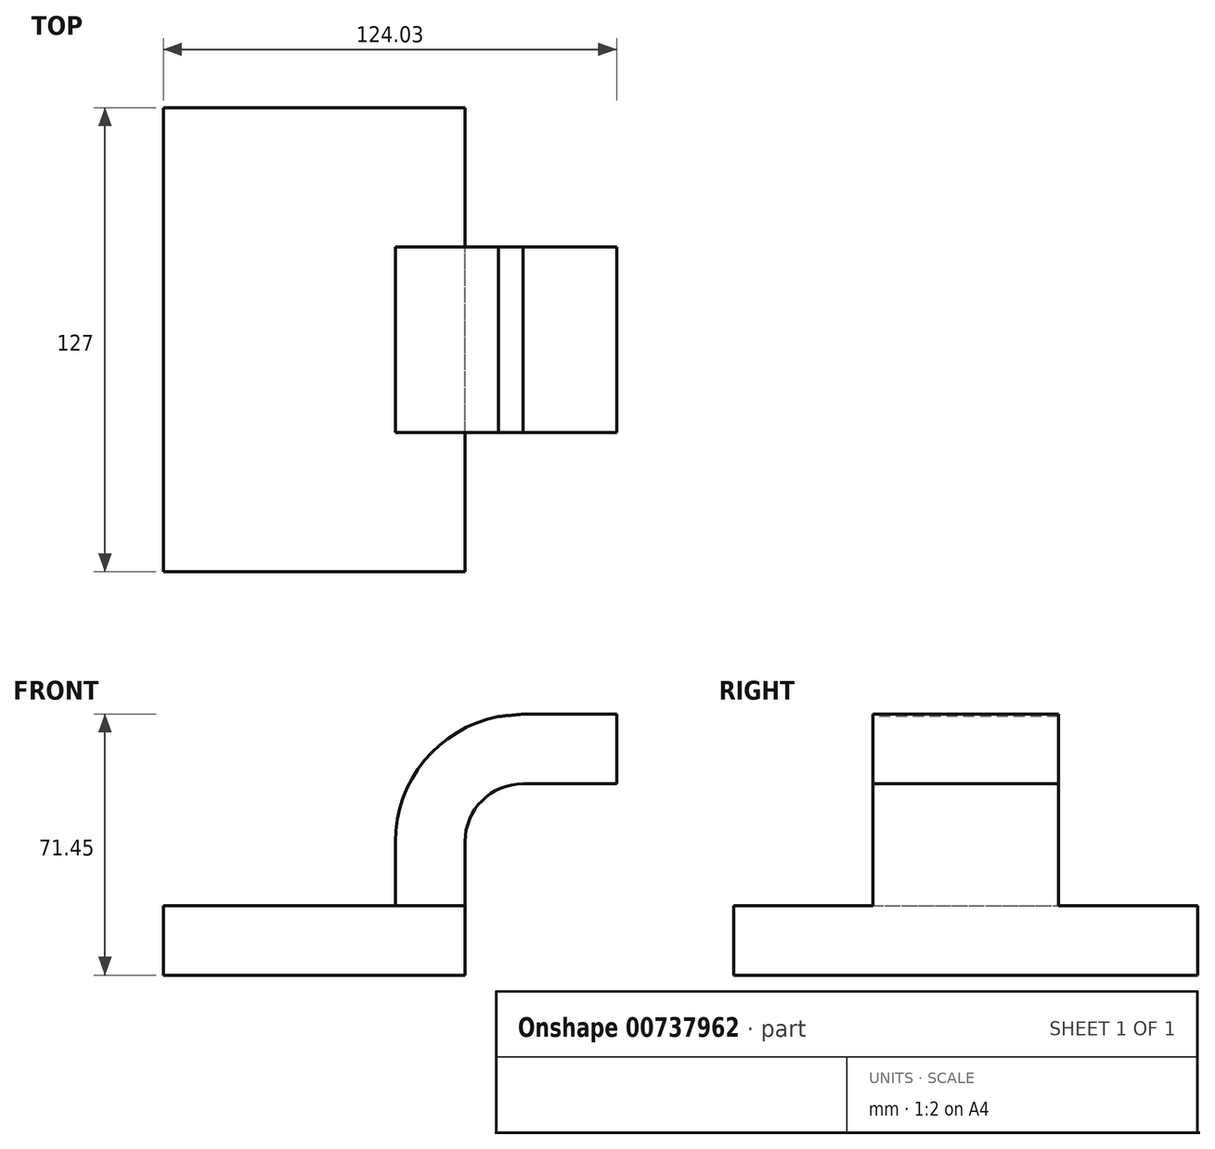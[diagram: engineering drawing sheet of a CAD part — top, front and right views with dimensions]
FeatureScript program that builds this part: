
annotation { "Feature Type Name" : "Feature", "Feature Type Description" : "" }
export const myFeature = defineFeature(function(context is Context, id is Id, definition is map)
    precondition{}
    {
        {
            var Q0;
            Q0=qCreatedBy(makeId("Front.planeOp"),FACE);
            var sketch = newSketch(context, id + "F0", { "sketchPlane" : qUnion([Q0])});
            skLineSegment(sketch, "E0.bottom", {"start": v(-29.35, 9.17) * mm, "end": v(53.2, 9.17) * mm});
            skLineSegment(sketch, "E0.top", {"start": v(-29.35, -9.88) * mm, "end": v(53.2, -9.88) * mm});
            skLineSegment(sketch, "E0.left", {"start": v(-29.35, 9.17) * mm, "end": v(-29.35, -9.88) * mm});
            skLineSegment(sketch, "E0.right", {"start": v(53.2, 9.17) * mm, "end": v(53.2, -9.88) * mm});
            skLineSegment(sketch, "E1", {"start": v(53.2, 9.17) * mm, "end": v(53.2, 26.64) * mm});
            skArc(sketch, "E2", {"start": v(53.2, 26.64) * mm, "mid": v(57.85, 37.87) * mm, "end": v(69.07, 42.52) * mm});
            skLineSegment(sketch, "E3.bottom", {"start": v(123.05, 66.32) * mm, "end": v(72.25, 66.32) * mm});
            skLineSegment(sketch, "E3.top", {"start": v(123.05, 37.74) * mm, "end": v(72.25, 37.74) * mm});
            skLineSegment(sketch, "E3.left", {"start": v(123.05, 66.32) * mm, "end": v(123.05, 37.74) * mm});
            skLineSegment(sketch, "E3.right", {"start": v(72.25, 66.32) * mm, "end": v(72.25, 37.74) * mm});
            skPoint(sketch, "E3.middle", {"position": v(97.65, 52.03) * mm});
            skLineSegment(sketch, "E4", {"start": v(69.07, 42.52) * mm, "end": v(94.68, 42.52) * mm});
            skLineSegment(sketch, "E5.0", {"start": v(69.07, 61.57) * mm, "end": v(94.68, 61.57) * mm});
            skArc(sketch, "E5.1", {"start": v(34.15, 26.64) * mm, "mid": v(44.38, 51.34) * mm, "end": v(69.07, 61.57) * mm});
            skLineSegment(sketch, "E5.2", {"start": v(34.15, 9.17) * mm, "end": v(34.15, 26.64) * mm});
            skLineSegment(sketch, "E6", {"start": v(94.68, 42.52) * mm, "end": v(94.68, 61.57) * mm});
            skLineSegment(sketch, "E7", {"start": v(94.68, 61.57) * mm, "end": v(94.68, 66.32) * mm});
            skLineSegment(sketch, "E8", {"start": v(94.68, 66.32) * mm, "end": v(94.68, 37.74) * mm});
            skFitSpline(sketch, "E9", {"points": [v(-29.35, 9.17) * mm, v(69.07, 61.57) * mm], "startDerivative": vector(51.04, 84.87) * mm, "endDerivative": vector(207.21, 18.59) * mm});
            skSolve(sketch);
        }
        {
            var Q0;
            Q0=makeQuery(id+"F0.imprint","IMPRINT",FACE,{"disambiguationData":[TD([[makeQuery(id+"F0.imprint","IMPRINT",EDGE,{"derivedFrom":sQuery(id+"F0.wireOp",EDGE,"E0.top")}),1.0]])]});
            extrude(context, id + "F1", {"entities" : qUnion([Q0]), "endBound" : BoundingType.SYMMETRIC, "depth" : 127 * mm, "offsetDistance" : 25.4 * mm});
        }
        {
            var Q0;
            {var subQ5=sQuery(id+"F0.wireOp",EDGE,"E1");Q0=makeQuery(id+"F0.imprint","IMPRINT",FACE,{"disambiguationData":[TD([[makeQuery(id+"F0.imprint","IMPRINT",EDGE,{"derivedFrom":subQ5}),1.0]])]});}
            var Q1;
            {var subQ0=sQuery(id+"F0.wireOp",EDGE,"E5.0");var subQ1=sQuery(id+"F0.wireOp",EDGE,"E3.right");var subQ2=makeQuery(id+"F0.imprint","INTERSECT",VERTEX,{"derivedFrom":[subQ1,subQ0]});Q1=makeQuery(id+"F0.imprint","IMPRINT",FACE,{"disambiguationData":[TD([[makeQuery(id+"F0.imprint","IMPRINT",EDGE,{"disambiguationData":[TD([[subQ2,-1.0]])],"derivedFrom":subQ1}),1.0]])]});}
            extrude(context, id + "F2", {"entities" : qUnion([Q0, Q1]), "operationType" : NewBodyOperationType.ADD, "endBound" : BoundingType.SYMMETRIC, "depth" : 50.8 * mm, "offsetDistance" : 25.4 * mm});
        }
    });
